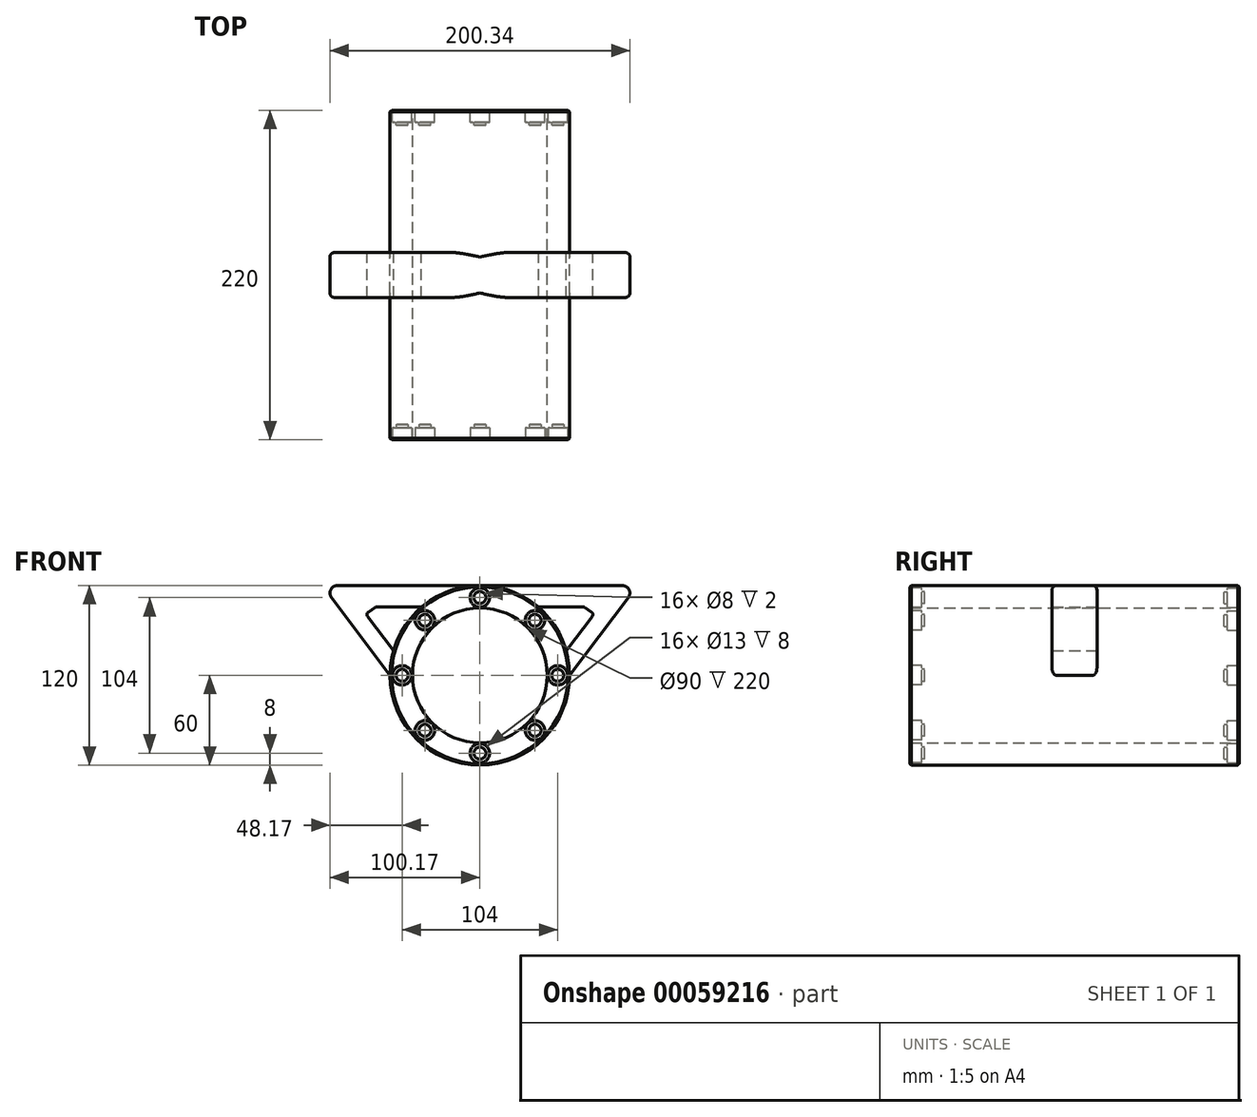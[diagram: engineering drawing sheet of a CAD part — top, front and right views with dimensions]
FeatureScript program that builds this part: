
annotation { "Feature Type Name" : "Feature", "Feature Type Description" : "" }
export const myFeature = defineFeature(function(context is Context, id is Id, definition is map)
    precondition{}
    {
        {
            var Q0;
            Q0=qCreatedBy(makeId("Front.planeOp"),FACE);
            var sketch = newSketch(context, id + "F0", { "sketchPlane" : qUnion([Q0])});
            skCircle(sketch, "E0", {"center": v(0, 0) * mm, "radius": 60 * mm});
            skCircle(sketch, "E1", {"center": v(0, 0) * mm, "radius": 45 * mm});
            skSolve(sketch);
        }
        {
            var Q0;
            Q0=makeQuery(id+"F0.imprint","IMPRINT",FACE,{"disambiguationData":[TD([[makeQuery(id+"F0.imprint","IMPRINT",EDGE,{"derivedFrom":sQuery(id+"F0.wireOp",EDGE,"E0")}),1.0]])]});
            extrude(context, id + "F1", {"entities" : qUnion([Q0]), "endBound" : BoundingType.SYMMETRIC, "depth" : 200 * mm});
        }
        {
            var Q0;
            Q0=qCreatedBy(makeId("Front.planeOp"),FACE);
            var sketch = newSketch(context, id + "F2", { "sketchPlane" : qUnion([Q0])});
            skCircle(sketch, "E2.0", {"center": v(0, 0) * mm, "radius": 60 * mm});
            skCircle(sketch, "E3.0", {"center": v(0, 0) * mm, "radius": 45 * mm});
            skLineSegment(sketch, "E4", {"start": v(0, 60) * mm, "end": v(91.53, 60) * mm, "construction": true});
            skLineSegment(sketch, "E5", {"start": v(99.16, 52) * mm, "end": v(60, 0) * mm});
            skLineSegment(sketch, "E6", {"start": v(60, 0) * mm, "end": v(0, 0) * mm});
            skLineSegment(sketch, "E7", {"start": v(95.17, 60) * mm, "end": v(0, 60) * mm});
            skPoint(sketch, "E8.visualSharp", {"position": v(105.2, 60) * mm});
            skArc(sketch, "E8.filletArc", {"start": v(99.16, 52) * mm, "mid": v(99.65, 57.23) * mm, "end": v(95.17, 60) * mm});
            skLineSegment(sketch, "E9", {"start": v(40.09, 45.77) * mm, "end": v(68.92, 45.77) * mm});
            skLineSegment(sketch, "E10", {"start": v(70.05, 45.41) * mm, "end": v(74.56, 42.32) * mm});
            skLineSegment(sketch, "E11", {"start": v(75.02, 39.47) * mm, "end": v(57.85, 16.66) * mm});
            skArc(sketch, "E12", {"start": v(54.26, 17.65) * mm, "mid": v(49.43, 31.6) * mm, "end": v(39.02, 42.08) * mm});
            skPoint(sketch, "E13.visualSharp", {"position": v(11.6, 45.77) * mm});
            skArc(sketch, "E13.filletArc", {"start": v(40.09, 45.77) * mm, "mid": v(38.17, 44.32) * mm, "end": v(39.02, 42.08) * mm});
            skPoint(sketch, "E14.visualSharp", {"position": v(54.4, 12.09) * mm});
            skArc(sketch, "E14.filletArc", {"start": v(54.26, 17.65) * mm, "mid": v(55.72, 15.94) * mm, "end": v(57.85, 16.66) * mm});
            skPoint(sketch, "E15.visualSharp", {"position": v(76.28, 41.13) * mm});
            skArc(sketch, "E15.filletArc", {"start": v(75.02, 39.47) * mm, "mid": v(75.4, 41) * mm, "end": v(74.56, 42.32) * mm});
            skPoint(sketch, "E16.visualSharp", {"position": v(69.54, 45.77) * mm});
            skArc(sketch, "E16.filletArc", {"start": v(70.05, 45.41) * mm, "mid": v(69.52, 45.68) * mm, "end": v(68.92, 45.77) * mm});
            skSolve(sketch);
        }
        {
            var Q0;
            {var subQ0=sQuery(id+"F2.wireOp",EDGE,"E5");Q0=makeQuery(id+"F2.imprint","IMPRINT",FACE,{"disambiguationData":[TD([[makeQuery(id+"F2.imprint","IMPRINT",EDGE,{"derivedFrom":subQ0}),-1.0]])]});}
            extrude(context, id + "F3", {"entities" : qUnion([Q0]), "operationType" : NewBodyOperationType.ADD, "endBound" : BoundingType.SYMMETRIC, "depth" : 30 * mm});
        }
        {
            var Q0;
            Q0=makeQuery(id+"F3.opExtrude","CAP_EDGE",EDGE,{"disambiguationData":[OSD([sQuery(id+"F2.wireOp",EDGE,"E7")])],"isStart":false});
            var Q1;
            Q1=makeQuery(id+"F3.opExtrude","CAP_EDGE",EDGE,{"disambiguationData":[OSD([sQuery(id+"F2.wireOp",EDGE,"E8.filletArc")])],"isStart":false});
            var Q2;
            Q2=makeQuery(id+"F3.opExtrude","CAP_EDGE",EDGE,{"disambiguationData":[OSD([sQuery(id+"F2.wireOp",EDGE,"E5")])],"isStart":true});
            var Q3;
            Q3=makeQuery(id+"F3.opExtrude","CAP_EDGE",EDGE,{"disambiguationData":[OSD([sQuery(id+"F2.wireOp",EDGE,"E2.0")])],"isStart":false});
            fillet(context, id + "F4", {"entities" : qUnion([Q0, Q1, Q2, Q3]), "radius" : 3 * mm, "tangentPropagation" : true, "allowEdgeOverflow" : false});
        }
        {
            var Q0;
            Q0=makeQuery(id+"F1.opExtrude","CAP_FACE",FACE,{"disambiguationData":[OSD([sQuery(id+"F0.wireOp",EDGE,"E0"),sQuery(id+"F0.wireOp",EDGE,"E1")])],"isStart":false});
            var sketch = newSketch(context, id + "F5", { "sketchPlane" : qUnion([Q0])});
            skCircle(sketch, "E17.0", {"center": v(0, 0) * mm, "radius": 60 * mm});
            skCircle(sketch, "E18.0", {"center": v(0, 0) * mm, "radius": 45 * mm});
            skSolve(sketch);
        }
        {
            var Q0;
            Q0=makeQuery(id+"F5.imprint","IMPRINT",FACE,{"disambiguationData":[TD([[makeQuery(id+"F5.imprint","IMPRINT",EDGE,{"derivedFrom":sQuery(id+"F5.wireOp",EDGE,"E17.0")}),1.0]])]});
            extrude(context, id + "F6", {"entities" : qUnion([Q0]), "depth" : 10 * mm});
        }
        {
            var Q0;
            Q0=makeQuery(id+"F6.opExtrude","CAP_EDGE",EDGE,{"disambiguationData":[OSD([sQuery(id+"F5.wireOp",EDGE,"E17.0")])],"isStart":false});
            chamfer(context, id + "F7", {"entities" : qUnion([Q0]), "width" : 1 * mm});
        }
        {
            var Q0;
            Q0=makeQuery(id+"F6.opExtrude","CAP_FACE",FACE,{"disambiguationData":[OSD([sQuery(id+"F5.wireOp",EDGE,"E17.0"),sQuery(id+"F5.wireOp",EDGE,"E17.1")])],"isStart":false});
            var sketch = newSketch(context, id + "F8", { "sketchPlane" : qUnion([Q0])});
            skCircle(sketch, "E19.0", {"center": v(0, 0) * mm, "radius": 59 * mm});
            skLineSegment(sketch, "E20", {"start": v(0, 45) * mm, "end": v(0, 59) * mm, "construction": true});
            skPoint(sketch, "E21", {"position": v(0, 52) * mm});
            skPoint(sketch, "E22.1.0", {"position": v(-36.77, 36.77) * mm});
            skPoint(sketch, "E22.2.0", {"position": v(-52, 0) * mm});
            skPoint(sketch, "E22.3.0", {"position": v(-36.77, -36.77) * mm});
            skPoint(sketch, "E22.4.0", {"position": v(0, -52) * mm});
            skPoint(sketch, "E22.5.0", {"position": v(36.77, -36.77) * mm});
            skPoint(sketch, "E22.6.0", {"position": v(52, 0) * mm});
            skPoint(sketch, "E22.7.0", {"position": v(36.77, 36.77) * mm});
            skCircle(sketch, "E23.0", {"center": v(0, 0) * mm, "radius": 45 * mm});
            skSolve(sketch);
        }
        {
            var Q0;
            Q0=sQuery(id+"F8.wireOp",VERTEX,"E21");
            var Q1;
            Q1=sQuery(id+"F8.wireOp",VERTEX,"E22.7.0");
            var Q2;
            Q2=sQuery(id+"F8.wireOp",VERTEX,"E22.6.0");
            var Q3;
            Q3=sQuery(id+"F8.wireOp",VERTEX,"E22.5.0");
            var Q4;
            Q4=sQuery(id+"F8.wireOp",VERTEX,"E22.4.0");
            var Q5;
            Q5=sQuery(id+"F8.wireOp",VERTEX,"E22.3.0");
            var Q6;
            Q6=sQuery(id+"F8.wireOp",VERTEX,"E22.2.0");
            var Q7;
            Q7=sQuery(id+"F8.wireOp",VERTEX,"E22.1.0");
            var Q8;
            Q8=makeQuery(id+"F6.opExtrude","SWEPT_BODY",BODY,{"disambiguationData":[OSD([sQuery(id+"F5.wireOp",EDGE,"E17.0"),sQuery(id+"F5.wireOp",EDGE,"E18.0")])]});
            hole(context, id + "F9", {"style" : HoleStyle.C_BORE, "holeDiameter" : 8 * mm, "cBoreDiameter" : 13 * mm, "cBoreDepth" : 8 * mm, "endStyle" : HoleEndStyle.BLIND, "holeDepth" : 20 * mm, "locations" : qUnion([Q0, Q1, Q2, Q3, Q4, Q5, Q6, Q7]), "scope" : qUnion([Q8])});
        }
        {
            var Q0;
            Q0=makeQuery(id+"F6.opExtrude","SWEPT_BODY",BODY,{"disambiguationData":[OSD([sQuery(id+"F5.wireOp",EDGE,"E17.0"),sQuery(id+"F5.wireOp",EDGE,"E17.1"),sQuery(id+"F5.wireOp",EDGE,"884e5bbf-b0c6-4582-a5ff-be8733ad6445"),sQuery(id+"F5.wireOp",EDGE,"84ca4d87-0559-42a4-a57a-d8909d35ff5c.1.0"),sQuery(id+"F5.wireOp",EDGE,"84ca4d87-0559-42a4-a57a-d8909d35ff5c.2.0"),sQuery(id+"F5.wireOp",EDGE,"84ca4d87-0559-42a4-a57a-d8909d35ff5c.3.0"),sQuery(id+"F5.wireOp",EDGE,"84ca4d87-0559-42a4-a57a-d8909d35ff5c.4.0"),sQuery(id+"F5.wireOp",EDGE,"84ca4d87-0559-42a4-a57a-d8909d35ff5c.5.0"),sQuery(id+"F5.wireOp",EDGE,"84ca4d87-0559-42a4-a57a-d8909d35ff5c.6.0"),sQuery(id+"F5.wireOp",EDGE,"84ca4d87-0559-42a4-a57a-d8909d35ff5c.7.0")])]});
            var Q1;
            Q1=qCreatedBy(makeId("Front.planeOp"),FACE);
            mirror(context, id + "F10", {"entities" : qUnion([Q0]), "mirrorPlane" : qUnion([Q1])});
        }
        {
            var Q0;
            Q0=makeQuery(id+"F1.opExtrude","SWEPT_BODY",BODY,{"disambiguationData":[OSD([sQuery(id+"F0.wireOp",EDGE,"E0"),sQuery(id+"F0.wireOp",EDGE,"E1")])]});
            var Q1;
            Q1=qCreatedBy(makeId("Right.planeOp"),FACE);
            mirror(context, id + "F11", {"operationType" : NewBodyOperationType.ADD, "entities" : qUnion([Q0]), "mirrorPlane" : qUnion([Q1])});
        }
    });
